# Revit family: WC-Connector-Caroma Junior 100 Suite1
name_source: partatom
category: Plumbing Fixtures
revit_build: Autodesk Revit 2014 (Build: 20131024_2115(x64)
units: mm (PartAtom-declared; Revit-internal decimal feet)

## types (1)
- Standard
    Assembly Code = D2010110
    CW Connection = Yes
    CWFU = 2
    Cost = 0 $
    Default Elevation = 0 mm  [stored 0 ft]
    Description = Caroma Junior 100 Connector Suite
    HW Connection = No
    Hardware = Metal-Chrome-Caroma
    Height_ANZRS = 881 mm  [stored 2.89042 ft]
    Keynote = WC
    Length_ANZRS = 630 mm  [stored 2.06693 ft]
    Manufacturer = GWA Bathrooms & Kitchens
    Material_ANZRS = Porcelain-White-Caroma
    Model = 984241W
    PlumbingMaterial_ANZRS = Porcelain-White-Caroma
    Type Comments = Pan specifically designed for infants, Adjustable junior connector style, S or P trap available, Bottom inlet cistern, Includes junior seat, Plastic cistern, Vitreous China Pan, White only
    URL = http://www.caroma.com.au
    Vent Connection = No
    WELSRating_ANZRS = WELS 4 star rated, 4.5/3L
    WFU = 3
    Waste Connection = Yes
    WasteOutlet_ANZRS = 0
    Width_ANZRS = 445 mm  [stored 1.45997 ft]

note: [stored X ft] marks values corroborated as IEEE doubles in the binary element streams (Revit-internal decimal feet)

## geometry (parser evidence)
native form markers: Blend x8, Sweep x3
no freeform markers — native parametric forms only
